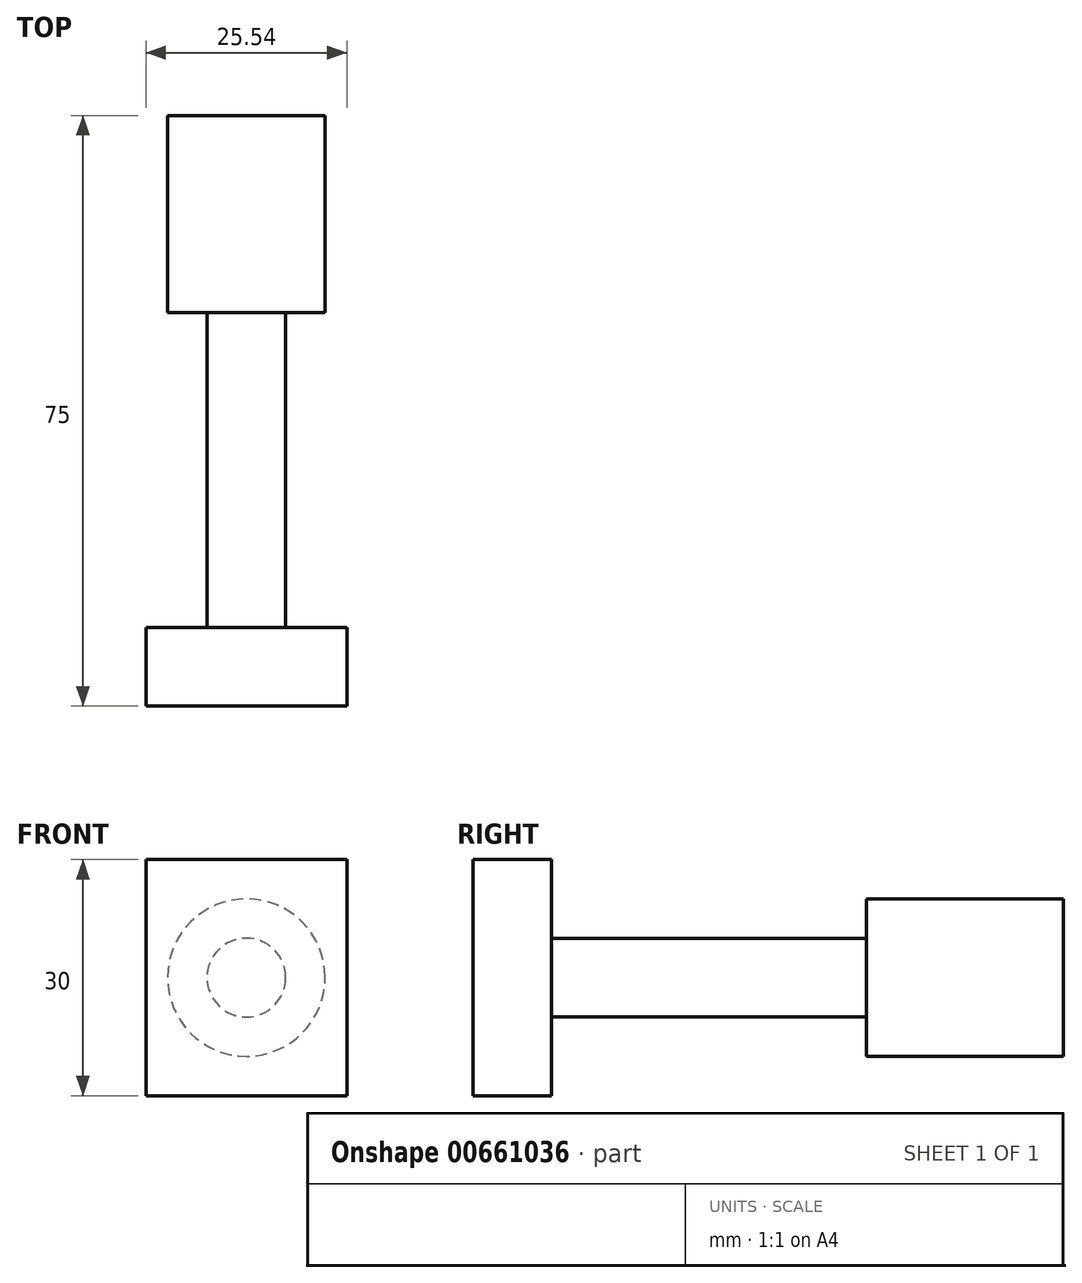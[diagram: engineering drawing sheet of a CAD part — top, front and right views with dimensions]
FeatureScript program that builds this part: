
annotation { "Feature Type Name" : "Feature", "Feature Type Description" : "" }
export const myFeature = defineFeature(function(context is Context, id is Id, definition is map)
    precondition{}
    {
        {
            var Q0;
            Q0=qCreatedBy(makeId("Front.planeOp"),FACE);
            var sketch = newSketch(context, id + "F0", { "sketchPlane" : qUnion([Q0])});
            skCircle(sketch, "E0", {"center": v(-28.65, 26.7) * mm, "radius": 10 * mm});
            skSolve(sketch);
        }
        {
            var Q0;
            Q0 = qSketchRegion(id + "F0", true);
            extrude(context, id + "F1", {"entities" : qUnion([Q0]), "depth" : 25 * mm, "offsetDistance" : 25 * mm});
        }
        {
            var Q0;
            Q0=makeQuery(id+"F1.opExtrude","CAP_FACE",FACE,{"disambiguationData":[OSD([sQuery(id+"F0.wireOp",EDGE,"E0")])],"isStart":false});
            var sketch = newSketch(context, id + "F2", { "sketchPlane" : qUnion([Q0])});
            skCircle(sketch, "E1", {"center": v(-28.65, 26.7) * mm, "radius": 5 * mm});
            skSolve(sketch);
        }
        {
            var Q0;
            Q0=makeQuery(id+"F2.imprint","IMPRINT",FACE,{"disambiguationData":[TD([[makeQuery(id+"F2.imprint","IMPRINT",EDGE,{"derivedFrom":sQuery(id+"F2.wireOp",EDGE,"E1")}),1.0]])]});
            extrude(context, id + "F3", {"entities" : qUnion([Q0]), "operationType" : NewBodyOperationType.ADD, "depth" : 40 * mm, "offsetDistance" : 25 * mm});
        }
        {
            var Q0;
            Q0=makeQuery(id+"F3.opExtrude","CAP_FACE",FACE,{"disambiguationData":[OSD([sQuery(id+"F2.wireOp",EDGE,"E1")])],"isStart":false});
            var sketch = newSketch(context, id + "F4", { "sketchPlane" : qUnion([Q0])});
            skLineSegment(sketch, "E2.bottom", {"start": v(-15.88, 11.7) * mm, "end": v(-41.42, 11.7) * mm});
            skLineSegment(sketch, "E2.top", {"start": v(-15.88, 41.7) * mm, "end": v(-41.42, 41.7) * mm});
            skLineSegment(sketch, "E2.left", {"start": v(-15.88, 11.7) * mm, "end": v(-15.88, 41.7) * mm});
            skLineSegment(sketch, "E2.right", {"start": v(-41.42, 11.7) * mm, "end": v(-41.42, 41.7) * mm});
            skPoint(sketch, "E2.middle", {"position": v(-28.65, 26.7) * mm});
            skSolve(sketch);
        }
        {
            var Q0;
            Q0 = qSketchRegion(id + "F4", true);
            extrude(context, id + "F5", {"entities" : qUnion([Q0]), "operationType" : NewBodyOperationType.ADD, "depth" : 10 * mm, "offsetDistance" : 25 * mm});
        }
    });
